# Revit family: QF_NuovAIR_N260T1-2D----
name_source: partatom
category: Specialty Equipment
units: mm (PartAtom-declared; Revit-internal decimal feet)

## family parameters
Always vertical = Yes
Cut with Voids When Loaded = No
Part Type = Normal
Room Calculation Point = No
Round Connector Dimension = Use Diameter
Shared = No
Work Plane-Based = No

## types (6) — shared parameters
Accessory = No
CE Approved = Yes
Conn Plug = terminal block
Depth Actual = 1350 mm  [stored 4.42913 ft]
Description = Blast Chiller, 40-20 tray GN1/1 - GN2/1- 60x40
Direct Waste Connection Height = 150 mm  [stored 0.492126 ft]
Direct Waste Size = 32 mm
Elec Connection Height = 2360 mm  [stored 7.74278 ft]
Electric power = 3000000 W
Foodservice Equipment Identifier = Yes
Height Actual = 2390 mm  [stored 7.84121 ft]
Identify Quantity as Lot = No
Item Number = N260T1
Keynote = 0
Length Actual = 1680 mm  [stored 5.51181 ft]
Main switch integrated = No
Manufacturer = NUOVAIR
Mat_Case = QF_Stainless-Brushed
Mat_Clearance = QF_Clearance
Mat_Legs = QF_Stainless-Brushed
Model = N260T1
Number of Poles = 3
Phase = 3
Potential Equalisation = Yes
Refrigerant Compressor Remote = Yes
Refrigerant Type = R452a
Refrigeration Liquid Line Size = 18 mm
Refrigeration Suction Line Size = 35 mm
URL Cutsheet = N260T1-en-1.pdf
URL Manufacturer = https://www.nuovair.com
Volt Free Conn = No
Weight = 600.00 kg

## per-type parameters (varying)
| type | Cycle | FL Amps | LH | RH | Volts |
| N260T1_LH_400V 50A | 50 Hz | 7 A | Yes | No | 400 V |
| N260T1_RH_400V 50A | 50 Hz | 7 A | No | Yes | 400 V |
| N260T1_LH_440V 60A | 60 Hz | 7 A | Yes | No | 440 V |
| N260T1_RH_440V 60A | 60 Hz | 7 A | No | Yes | 440 V |
| N260T1_LH_230V 60A | 60 Hz | 14 A | Yes | No | 230 V |
| N260T1_RH_230V 60A | 60 Hz | 14 A | No | Yes | 230 V |

note: [stored X ft] marks values corroborated as IEEE doubles in the binary element streams (Revit-internal decimal feet)

## geometry (parser evidence)
native form markers: Sweep x7
no freeform markers — native parametric forms only
